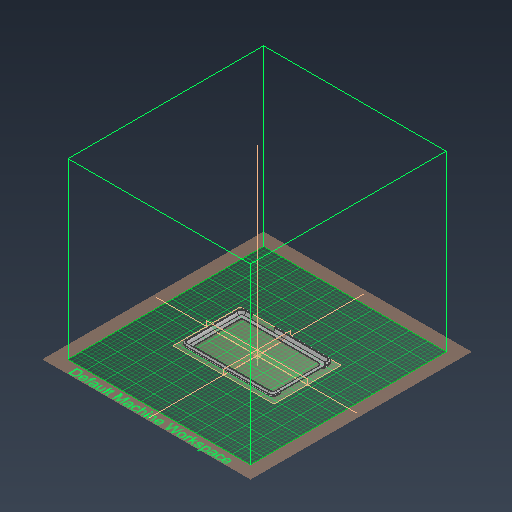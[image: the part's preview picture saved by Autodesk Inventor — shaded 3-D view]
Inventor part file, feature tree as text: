
AUTODESK INVENTOR PART (.ipt)
format: ipt  version: 2021 (Build 250183000, 183)  size: 1,605,120 bytes
history: native  units: mm
features: other x7, extrude x4, fillet x4, sketch x4, plane x2, thicken_offset x1, chamfer x1, surface_op x1
ambient origin geometry x8: Origin, YZ Plane, XZ Plane, XY Plane, X Axis, Y Axis, Z Axis, Center Point
bodies: Solid1 (feature_tree), Solid2 (feature_tree)
feature tree (24):
  extrude  "Extrusion1"  Depth=137.5mm
  fillet  "Fillet1"  [1 undecoded]
  fillet  "Fillet2"  Radius=9.9mm
  fillet  "Fillet3"  Radius=1.46mm
  thicken_offset  "Thicken1"
  chamfer  "Chamfer2"  [1 undecoded]
  extrude  "Extrusion2"  Depth=6.0mm TaperAngle=0.0deg
  plane  "Work Plane1"
  plane  "Work Plane2"
  other  "Ruled Surface6"
  surface_op  "Sculpt1"
  extrude  "Extrusion3"  Depth=6.0mm TaperAngle=0.0deg
  extrude  "Extrusion5"  Depth=5.9mm
  fillet  "Fillet5"  Radius=2.0mm
  sketch  "Sketch1"  dims[d0=208.4mm d1=137.5mm d3=0.0mm d4=9.9mm d7=1.46mm d8=0.8mm d18=0.0mm d19=0.0mm]
  sketch  "Sketch3"  dims[d20=53.5mm d22=6.0mm d23=0.0mm]
  sketch  "Sketch4"  dims[d28=5.9mm d29=6.0mm d30=0.0mm d31=5.9mm d32=2.0mm d33=2.0mm d34=3.5mm d35=10.0mm d36=3.5mm d37=10.0mm d38=5.0mm d39=0.0mm d40=5.0mm d41=10.0mm d42=8.0mm d43=8.0mm d44=8.0mm d45=8.0mm d46=5.9mm d47=24.5mm d48=19.0mm d49=19.0mm d53=0.5mm d54=2.0mm d55=45.0deg d87=10.0mm d88=5.585054mm d89=10.0mm d90=0.0mm d91=10.0mm d92=45.0deg d108=2.0mm]
  other  "Srf7"
  other  "Ruled Surface7"
  other  "Srf8"
  sketch  "3D Sketch9"
  other  "Ruled Surface8"
  other  "Srf9"
  other  "3D Intersection3"
note: 2 required parameter values undecoded (feature->parameter linkage not recoverable at this tier; creation-order binding heuristic only, values carry confidence <= 0.55)
